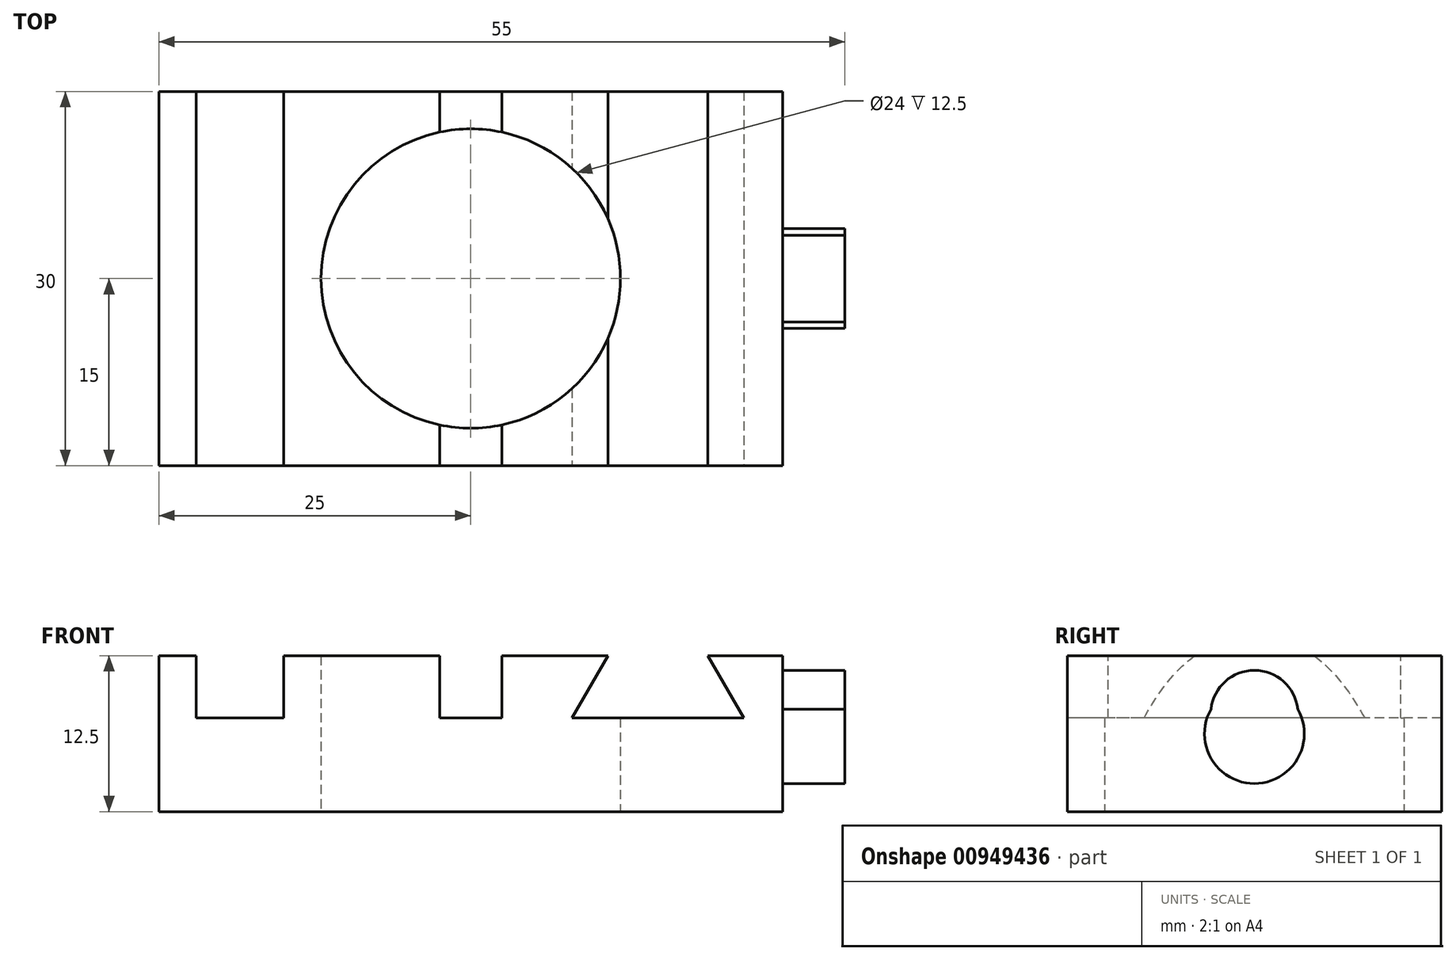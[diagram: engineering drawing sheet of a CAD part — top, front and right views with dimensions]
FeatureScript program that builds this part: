
annotation { "Feature Type Name" : "Feature", "Feature Type Description" : "" }
export const myFeature = defineFeature(function(context is Context, id is Id, definition is map)
    precondition{}
    {
        {
            var Q0;
            Q0=qCreatedBy(makeId("Top.planeOp"),FACE);
            var sketch = newSketch(context, id + "F0", { "sketchPlane" : qUnion([Q0])});
            skLineSegment(sketch, "E0.bottom", {"start": v(25, -15) * mm, "end": v(-25, -15) * mm});
            skLineSegment(sketch, "E0.top", {"start": v(25, 15) * mm, "end": v(-25, 15) * mm});
            skLineSegment(sketch, "E0.left", {"start": v(25, -15) * mm, "end": v(25, 15) * mm});
            skLineSegment(sketch, "E0.right", {"start": v(-25, -15) * mm, "end": v(-25, 15) * mm});
            skPoint(sketch, "E0.middle", {"position": v(0, 0) * mm});
            skCircle(sketch, "E1", {"center": v(0, 0) * mm, "radius": 12 * mm});
            skSolve(sketch);
        }
        {
            var Q0;
            Q0=makeQuery(id+"F0.imprint","IMPRINT",FACE,{"disambiguationData":[TD([[makeQuery(id+"F0.imprint","IMPRINT",EDGE,{"derivedFrom":sQuery(id+"F0.wireOp",EDGE,"E0.bottom")}),-1.0]])]});
            extrude(context, id + "F1", {"entities" : qUnion([Q0]), "depth" : 12.5 * mm, "offsetDistance" : 25 * mm});
        }
        {
            var Q0;
            Q0=makeQuery(id+"F1.opExtrude","CAP_FACE",FACE,{"disambiguationData":[OSD([sQuery(id+"F0.wireOp",EDGE,"E0.bottom"),sQuery(id+"F0.wireOp",EDGE,"E0.top"),sQuery(id+"F0.wireOp",EDGE,"E0.left"),sQuery(id+"F0.wireOp",EDGE,"E0.right"),sQuery(id+"F0.wireOp",EDGE,"E1")])],"isStart":false});
            var sketch = newSketch(context, id + "F2", { "sketchPlane" : qUnion([Q0])});
            skLineSegment(sketch, "E2.bottom", {"start": v(-22, 15) * mm, "end": v(-15, 15) * mm});
            skLineSegment(sketch, "E2.top", {"start": v(-22, -15) * mm, "end": v(-15, -15) * mm});
            skLineSegment(sketch, "E2.left", {"start": v(-22, 15) * mm, "end": v(-22, -15) * mm});
            skLineSegment(sketch, "E2.right", {"start": v(-15, 15) * mm, "end": v(-15, -15) * mm});
            skLineSegment(sketch, "E3", {"start": v(-2.5, 15) * mm, "end": v(-2.5, -15) * mm});
            skLineSegment(sketch, "E4", {"start": v(-2.5, -15) * mm, "end": v(2.5, -15) * mm});
            skLineSegment(sketch, "E5", {"start": v(2.5, -15) * mm, "end": v(2.5, 15) * mm});
            skLineSegment(sketch, "E6", {"start": v(2.5, 15) * mm, "end": v(-2.5, 15) * mm});
            skPoint(sketch, "E7", {"position": v(0, 0) * mm});
            skLineSegment(sketch, "E8", {"start": v(0, 15) * mm, "end": v(0, -15) * mm, "construction": true});
            skSolve(sketch);
        }
        {
            var Q0;
            Q0=makeQuery(id+"F2.imprint","IMPRINT",FACE,{"disambiguationData":[TD([[makeQuery(id+"F2.imprint","IMPRINT",EDGE,{"derivedFrom":sQuery(id+"F2.wireOp",EDGE,"E2.bottom")}),1.0]])]});
            var Q1;
            {var subQ0=sQuery(id+"F2.wireOp",EDGE,"E6");Q1=makeQuery(id+"F2.imprint","IMPRINT",FACE,{"disambiguationData":[TD([[makeQuery(id+"F2.imprint","IMPRINT",EDGE,{"derivedFrom":subQ0}),1.0]])]});}
            var Q2;
            {var subQ0=sQuery(id+"F2.wireOp",EDGE,"E4");Q2=makeQuery(id+"F2.imprint","IMPRINT",FACE,{"disambiguationData":[TD([[makeQuery(id+"F2.imprint","IMPRINT",EDGE,{"derivedFrom":subQ0}),-1.0]])]});}
            extrude(context, id + "F3", {"entities" : qUnion([Q0, Q1, Q2]), "operationType" : NewBodyOperationType.REMOVE, "oppositeDirection" : true, "depth" : 5 * mm, "offsetDistance" : 25 * mm});
        }
        {
            var Q0;
            Q0=makeQuery(id+"F1.opExtrude","SWEPT_FACE",FACE,{"disambiguationData":[OSD([sQuery(id+"F0.wireOp",EDGE,"E0.bottom")])]});
            var sketch = newSketch(context, id + "F4", { "sketchPlane" : qUnion([Q0])});
            skLineSegment(sketch, "E9", {"start": v(11, 12.5) * mm, "end": v(8.11, 7.5) * mm});
            skLineSegment(sketch, "E10", {"start": v(8.11, 7.5) * mm, "end": v(21.89, 7.5) * mm});
            skLineSegment(sketch, "E11", {"start": v(21.89, 7.5) * mm, "end": v(19, 12.5) * mm});
            skLineSegment(sketch, "E12", {"start": v(19, 12.5) * mm, "end": v(11, 12.5) * mm});
            skLineSegment(sketch, "E13", {"start": v(15, 7.5) * mm, "end": v(15, 12.5) * mm, "construction": true});
            skSolve(sketch);
        }
        {
            var Q0;
            Q0=makeQuery(id+"F4.imprint","IMPRINT",FACE,{"disambiguationData":[TD([[makeQuery(id+"F4.imprint","IMPRINT",EDGE,{"derivedFrom":sQuery(id+"F4.wireOp",EDGE,"E9")}),1.0]])]});
            extrude(context, id + "F5", {"entities" : qUnion([Q0]), "operationType" : NewBodyOperationType.REMOVE, "endBound" : BoundingType.THROUGH_ALL, "oppositeDirection" : true, "depth" : 25 * mm, "offsetDistance" : 25 * mm});
        }
        {
            var Q0;
            Q0=makeQuery(id+"F1.opExtrude","SWEPT_FACE",FACE,{"disambiguationData":[OSD([sQuery(id+"F0.wireOp",EDGE,"E0.left")])]});
            var sketch = newSketch(context, id + "F6", { "sketchPlane" : qUnion([Q0])});
            skCircle(sketch, "E14", {"center": v(0, 6.25) * mm, "radius": 4 * mm});
            skPoint(sketch, "E14.centerSnap0", {"position": v(-15, 6.25) * mm});
            skPoint(sketch, "E14.centerSnap1", {"position": v(0, 12.5) * mm});
            skSolve(sketch);
        }
        {
            var Q0;
            Q0=makeQuery(id+"F6.imprint","IMPRINT",FACE,{"disambiguationData":[TD([[makeQuery(id+"F6.imprint","IMPRINT",EDGE,{"derivedFrom":sQuery(id+"F6.wireOp",EDGE,"E14")}),1.0]])]});
            extrude(context, id + "F7", {"entities" : qUnion([Q0]), "operationType" : NewBodyOperationType.ADD, "depth" : 5 * mm, "offsetDistance" : 25 * mm});
        }
        {
            var Q0;
            Q0=makeQuery(id+"F1.opExtrude","SWEPT_FACE",FACE,{"disambiguationData":[OSD([sQuery(id+"F0.wireOp",EDGE,"E0.left")])]});
            var sketch = newSketch(context, id + "F8", { "sketchPlane" : qUnion([Q0])});
            skCircle(sketch, "E15", {"center": v(0, 6.25) * mm, "radius": 4 * mm});
            skPoint(sketch, "E15.centerSnap0", {"position": v(-15, 6.25) * mm});
            skPoint(sketch, "E15.centerSnap1", {"position": v(0, 12.5) * mm});
            skSolve(sketch);
        }
        {
            var Q0;
            Q0=makeQuery(id+"F8.imprint","IMPRINT",FACE,{"disambiguationData":[TD([[makeQuery(id+"F8.imprint","IMPRINT",EDGE,{"derivedFrom":sQuery(id+"F8.wireOp",EDGE,"E15")}),1.0]])]});
            extrude(context, id + "F9", {"entities" : qUnion([Q0]), "operationType" : NewBodyOperationType.ADD, "depth" : 5 * mm, "offsetDistance" : 25 * mm});
        }
        {
            var Q0;
            Q0=makeQuery(id+"F1.opExtrude","SWEPT_FACE",FACE,{"disambiguationData":[OSD([sQuery(id+"F0.wireOp",EDGE,"E0.left")])]});
            var sketch = newSketch(context, id + "F10", { "sketchPlane" : qUnion([Q0])});
            skCircle(sketch, "E16", {"center": v(0, 7.83) * mm, "radius": 3.5 * mm});
            skPoint(sketch, "E16.centerSnap0", {"position": v(0, 12.5) * mm});
            skSolve(sketch);
        }
        {
            var Q0;
            Q0=makeQuery(id+"F10.imprint","IMPRINT",FACE,{"disambiguationData":[TD([[makeQuery(id+"F10.imprint","IMPRINT",EDGE,{"derivedFrom":sQuery(id+"F10.wireOp",EDGE,"E16")}),1.0]])]});
            extrude(context, id + "F11", {"entities" : qUnion([Q0]), "operationType" : NewBodyOperationType.ADD, "depth" : 5 * mm, "offsetDistance" : 25 * mm});
        }
    });
